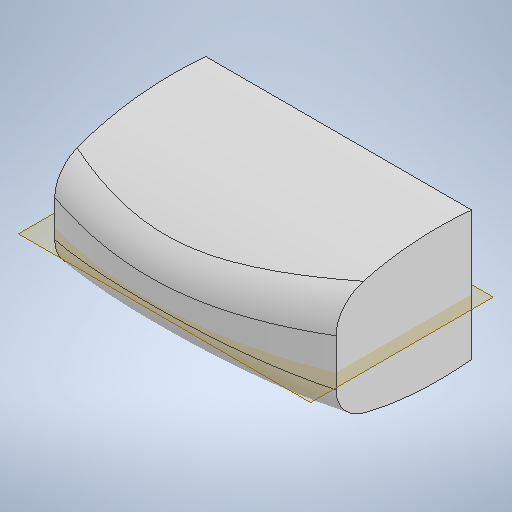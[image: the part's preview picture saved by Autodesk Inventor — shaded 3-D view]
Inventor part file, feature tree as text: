
AUTODESK INVENTOR PART (.ipt)
format: ipt  version: 2025 (Build 290162000, 162)  size: 299,008 bytes
history: native  units: in
note: dims shown in document units (in); Inventor stores cm internally (conversion verified against a paired STEP export)
features: extrude x3, sketch x3, other x2, fillet x1, projected_geometry x1
ambient origin geometry x8: Origin, YZ Plane, XZ Plane, XY Plane, X Axis, Y Axis, Z Axis, Center Point
bodies: Body1 (feature_tree)
feature tree (10):
  other  "ソリッド1"
  extrude  "押し出し1"  Depth=3.1496in
  other  "作業平面1"
  extrude  "押し出し2"  Depth=1.9685in
  extrude  "押し出し3"  Depth=0.2756in
  fillet  "フィレット2"  Radius=9.8425in
  sketch  "スケッチ1"
  sketch  "スケッチ2"
  projected_geometry  "投影ループ1"
  sketch  "スケッチ3"
